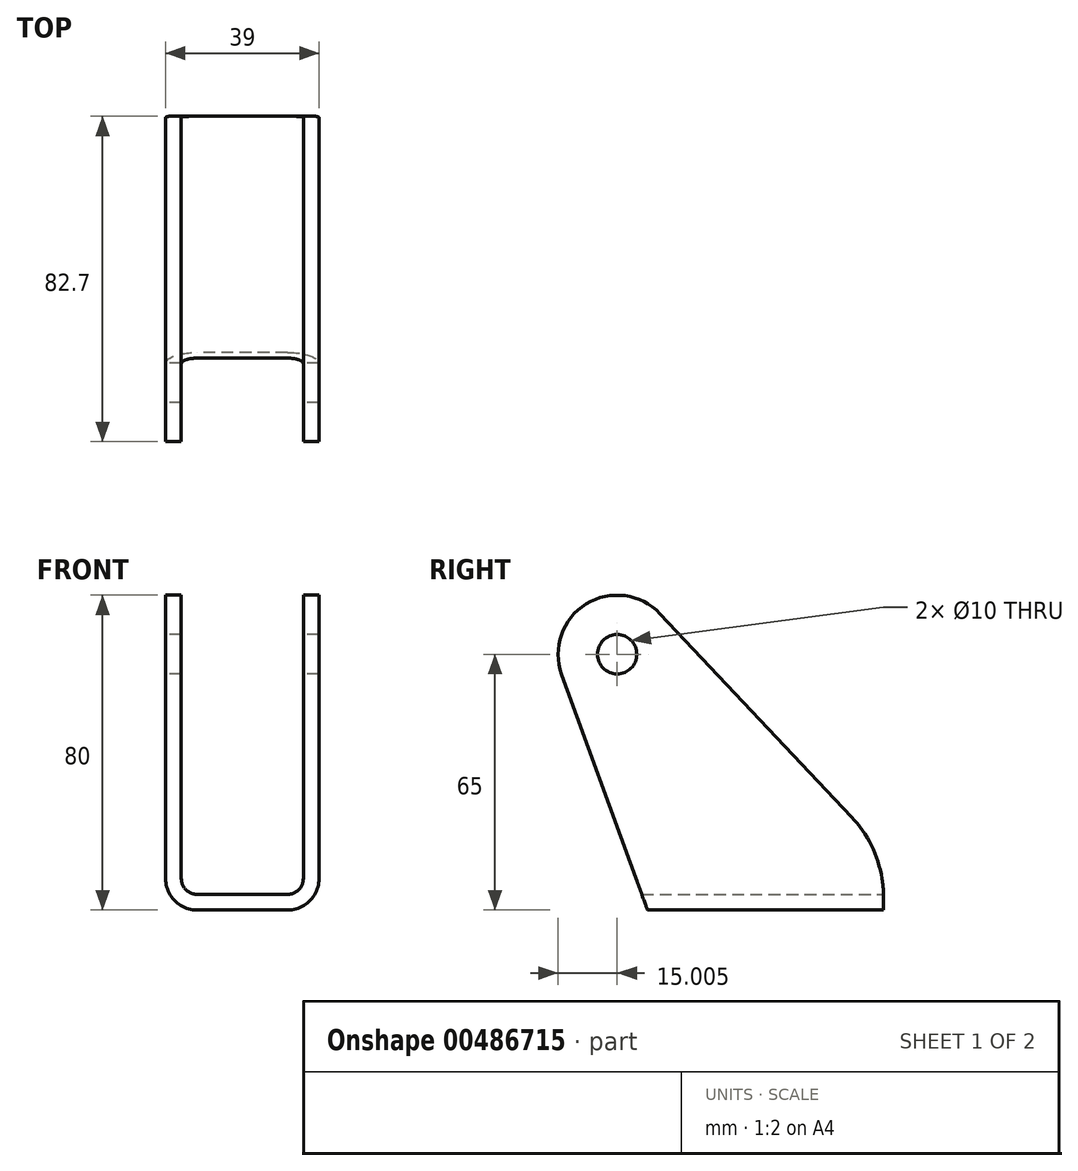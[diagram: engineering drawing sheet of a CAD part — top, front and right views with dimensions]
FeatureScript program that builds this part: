
annotation { "Feature Type Name" : "Feature", "Feature Type Description" : "" }
export const myFeature = defineFeature(function(context is Context, id is Id, definition is map)
    precondition{}
    {
        {
            var Q0;
            Q0=qCreatedBy(makeId("Right.planeOp"),FACE);
            var sketch = newSketch(context, id + "F0", { "sketchPlane" : qUnion([Q0])});
            skLineSegment(sketch, "E0", {"start": v(0, 0) * mm, "end": v(-21.8, 59.87) * mm});
            skLineSegment(sketch, "E1", {"start": v(0, 0) * mm, "end": v(60, 0) * mm});
            skLineSegment(sketch, "E2", {"start": v(60, 0) * mm, "end": v(60, 15) * mm});
            skArc(sketch, "E3", {"start": v(-21.8, 59.87) * mm, "mid": v(-15.56, 77.77) * mm, "end": v(3.22, 75.28) * mm});
            skCircle(sketch, "E4", {"center": v(-7.7, 65) * mm, "radius": 5 * mm});
            skLineSegment(sketch, "E5", {"start": v(3.22, 75.28) * mm, "end": v(60, 15) * mm});
            skSolve(sketch);
        }
        {
            var Q0;
            Q0=makeQuery(id+"F0.imprint","IMPRINT",FACE,{"disambiguationData":[TD([[makeQuery(id+"F0.imprint","IMPRINT",EDGE,{"derivedFrom":sQuery(id+"F0.wireOp",EDGE,"E0")}),-1.0]])]});
            extrude(context, id + "F1", {"entities" : qUnion([Q0]), "depth" : 39 * mm});
        }
        {
            var Q0;
            Q0=makeQuery(id+"F1.opExtrude","CAP_EDGE",EDGE,{"disambiguationData":[OSD([sQuery(id+"F0.wireOp",EDGE,"E1")])],"isStart":false});
            var Q1;
            Q1=makeQuery(id+"F1.opExtrude","CAP_EDGE",EDGE,{"disambiguationData":[OSD([sQuery(id+"F0.wireOp",EDGE,"E1")])],"isStart":true});
            fillet(context, id + "F2", {"entities" : qUnion([Q0, Q1]), "radius" : 8 * mm, "tangentPropagation" : true, "allowEdgeOverflow" : false});
        }
        {
            var Q0;
            {var subQ0=sQuery(id+"F0.wireOp",EDGE,"E5");var subQ1=sQuery(id+"F0.wireOp",EDGE,"E2");Q0=makeQuery(id+"FAPrw3ZTYDAtg6t_1.boolean.opBoolean","SPLIT",EDGE,{"disambiguationData":[TD([makeQuery(id+"FAPrw3ZTYDAtg6t_1.opExtrude","SWEPT_FACE",FACE,{"disambiguationData":[OSD([sQuery(id+"FQIFv68JuJi9x5a_1.wireOp",EDGE,"24cLHn3i-aFa6-R6zu-fpPz-IjsdmSHECpGQ")])]})])],"derivedFrom":makeQuery(id+"F1.opExtrude","SWEPT_EDGE",EDGE,{"disambiguationData":[OSD([subQ1,subQ0])]})});}
            var Q1;
            {var subQ0=sQuery(id+"F0.wireOp",EDGE,"E5");var subQ1=sQuery(id+"F0.wireOp",EDGE,"E2");Q1=makeQuery(id+"FAPrw3ZTYDAtg6t_1.boolean.opBoolean","SPLIT",EDGE,{"disambiguationData":[TD([makeQuery(id+"FAPrw3ZTYDAtg6t_1.opExtrude","SWEPT_FACE",FACE,{"disambiguationData":[OSD([sQuery(id+"FQIFv68JuJi9x5a_1.wireOp",EDGE,"Xe47tLbs-SprE-bTfk-mxtj-zssCxze5oTBk")])]})])],"derivedFrom":makeQuery(id+"F1.opExtrude","SWEPT_EDGE",EDGE,{"disambiguationData":[OSD([subQ1,subQ0])]})});}
            fillet(context, id + "F3", {"entities" : qUnion([Q0, Q1]), "radius" : 30 * mm, "tangentPropagation" : true, "allowEdgeOverflow" : false});
        }
        {
            var Q0;
            Q0=makeQuery(id+"F1.opExtrude","SWEPT_FACE",FACE,{"disambiguationData":[OSD([sQuery(id+"F0.wireOp",EDGE,"E2")])]});
            var sketch = newSketch(context, id + "F4", { "sketchPlane" : qUnion([Q0])});
            skLineSegment(sketch, "E6", {"start": v(-35, 4) * mm, "end": v(-4, 4) * mm});
            skLineSegment(sketch, "E7", {"start": v(-4, 4) * mm, "end": v(-4, 104) * mm});
            skLineSegment(sketch, "E8", {"start": v(-4, 104) * mm, "end": v(-35, 104) * mm});
            skLineSegment(sketch, "E9", {"start": v(-35, 104) * mm, "end": v(-35, 4) * mm});
            skSolve(sketch);
        }
        {
            var Q0;
            Q0=makeQuery(id+"F4.imprint","IMPRINT",FACE,{"disambiguationData":[TD([[makeQuery(id+"F4.imprint","IMPRINT",EDGE,{"derivedFrom":sQuery(id+"F4.wireOp",EDGE,"E6")}),1.0]])]});
            extrude(context, id + "F5", {"entities" : qUnion([Q0]), "operationType" : NewBodyOperationType.REMOVE, "endBound" : BoundingType.THROUGH_ALL, "oppositeDirection" : true, "depth" : 25 * mm});
        }
        {
            var Q0;
            Q0=makeQuery(id+"F5.boolean.opBoolean","COPY",EDGE,{"derivedFrom":makeQuery(id+"F5.opExtrude","SWEPT_EDGE",EDGE,{"disambiguationData":[OSD([sQuery(id+"F4.wireOp",EDGE,"E6"),sQuery(id+"F4.wireOp",EDGE,"E9")])]})});
            var Q1;
            Q1=makeQuery(id+"F5.boolean.opBoolean","COPY",EDGE,{"derivedFrom":makeQuery(id+"F5.opExtrude","SWEPT_EDGE",EDGE,{"disambiguationData":[OSD([sQuery(id+"F4.wireOp",EDGE,"E6"),sQuery(id+"F4.wireOp",EDGE,"E7")])]})});
            fillet(context, id + "F6", {"entities" : qUnion([Q0, Q1]), "radius" : 4 * mm, "tangentPropagation" : true, "allowEdgeOverflow" : false});
        }
    });
